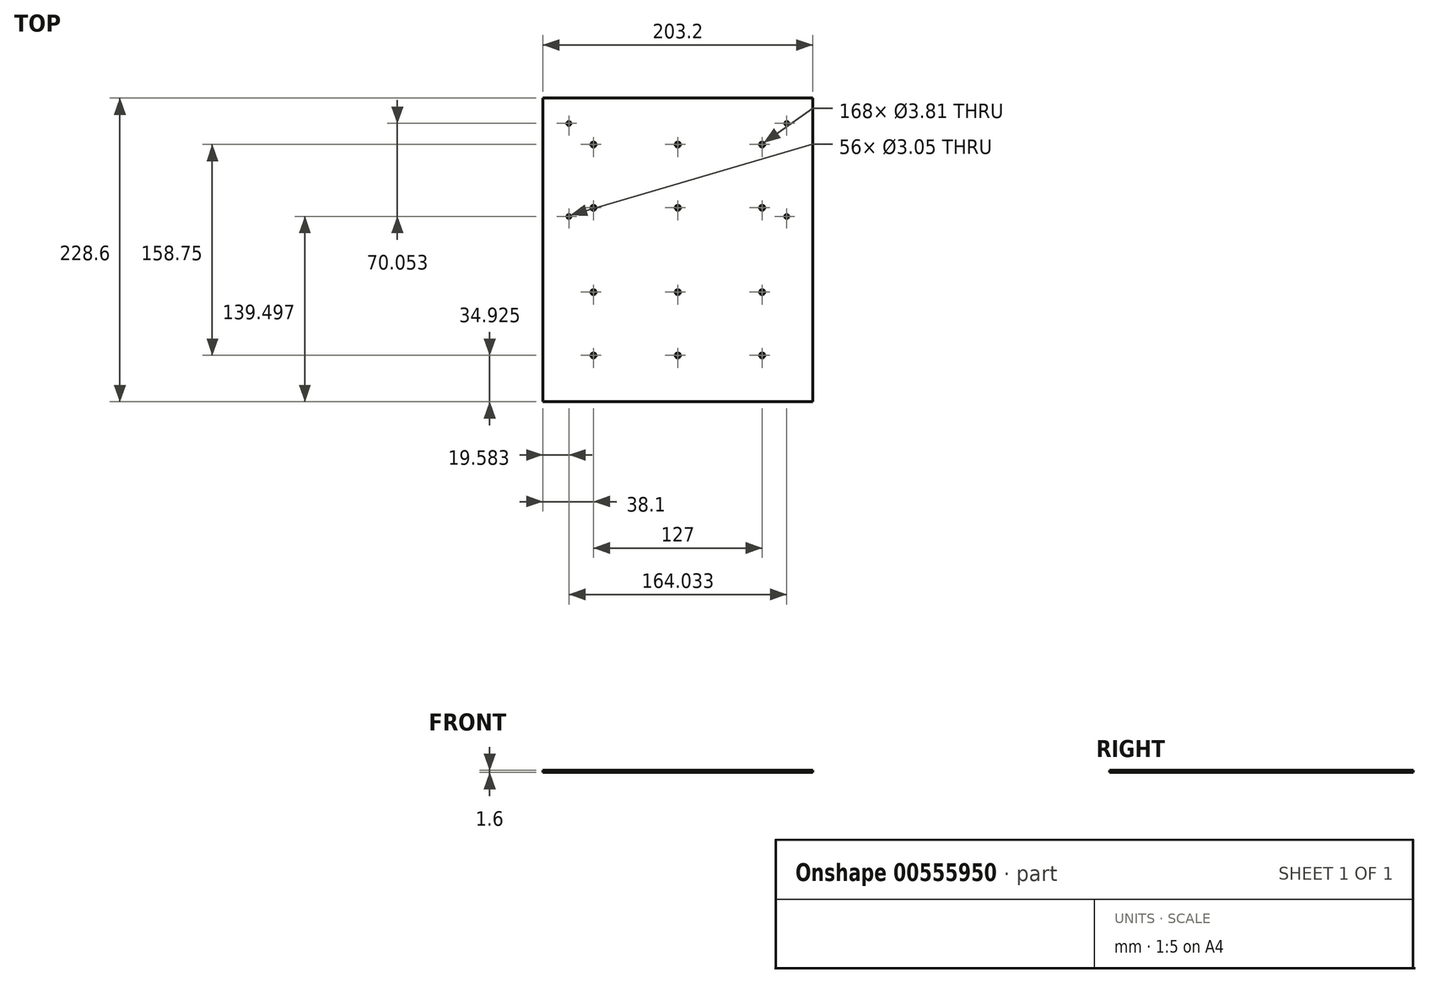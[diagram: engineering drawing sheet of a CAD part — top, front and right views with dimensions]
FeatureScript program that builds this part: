
annotation { "Feature Type Name" : "Feature", "Feature Type Description" : "" }
export const myFeature = defineFeature(function(context is Context, id is Id, definition is map)
    precondition{}
    {
        {
            var Q0;
            Q0=qCreatedBy(makeId("Top.planeOp"),FACE);
            var sketch = newSketch(context, id + "F0", { "sketchPlane" : qUnion([Q0])});
            skLineSegment(sketch, "E0.bottom", {"start": v(0, 0) * mm, "end": v(203.2, 0) * mm});
            skLineSegment(sketch, "E0.top", {"start": v(0, 228.6) * mm, "end": v(203.2, 228.6) * mm});
            skLineSegment(sketch, "E0.left", {"start": v(0, 0) * mm, "end": v(0, 228.6) * mm});
            skLineSegment(sketch, "E0.right", {"start": v(203.2, 0) * mm, "end": v(203.2, 228.6) * mm});
            skSolve(sketch);
        }
        {
            var Q0;
            Q0=makeQuery(id+"F0.imprint","IMPRINT",FACE,{"disambiguationData":[TD([[makeQuery(id+"F0.imprint","IMPRINT",EDGE,{"derivedFrom":sQuery(id+"F0.wireOp",EDGE,"E0.bottom")}),1.0]])]});
            extrude(context, id + "F1", {"entities" : qUnion([Q0]), "depth" : 1.6 * mm, "offsetDistance" : 25.4 * mm});
        }
        {
            var Q0;
            Q0=makeQuery(id+"F1.opExtrude","CAP_FACE",FACE,{"disambiguationData":[OSD([sQuery(id+"F0.wireOp",EDGE,"E0.bottom"),sQuery(id+"F0.wireOp",EDGE,"E0.top"),sQuery(id+"F0.wireOp",EDGE,"E0.left"),sQuery(id+"F0.wireOp",EDGE,"E0.right")])],"isStart":false});
            var sketch = newSketch(context, id + "F2", { "sketchPlane" : qUnion([Q0])});
            skCircle(sketch, "E1", {"center": v(19.58, 209.55) * mm, "radius": 1.52 * mm});
            skCircle(sketch, "E2", {"center": v(183.62, 209.55) * mm, "radius": 1.52 * mm});
            skCircle(sketch, "E3", {"center": v(19.58, 139.5) * mm, "radius": 1.52 * mm});
            skCircle(sketch, "E4", {"center": v(183.62, 139.5) * mm, "radius": 1.52 * mm});
            skSolve(sketch);
        }
        {
            var Q0;
            Q0 = qSketchRegion(id + "F2", true);
            extrude(context, id + "F3", {"entities" : qUnion([Q0]), "operationType" : NewBodyOperationType.REMOVE, "endBound" : BoundingType.THROUGH_ALL, "oppositeDirection" : true, "depth" : 25.4 * mm, "offsetDistance" : 25.4 * mm});
        }
        {
            var Q0;
            Q0=makeQuery(id+"F1.opExtrude","CAP_FACE",FACE,{"disambiguationData":[OSD([sQuery(id+"F0.wireOp",EDGE,"E0.bottom"),sQuery(id+"F0.wireOp",EDGE,"E0.top"),sQuery(id+"F0.wireOp",EDGE,"E0.left"),sQuery(id+"F0.wireOp",EDGE,"E0.right")])],"isStart":false});
            var sketch = newSketch(context, id + "F4", { "sketchPlane" : qUnion([Q0])});
            skCircle(sketch, "E5", {"center": v(165.1, 34.93) * mm, "radius": 1.9 * mm});
            skCircle(sketch, "E6.0.1.0", {"center": v(165.1, 82.55) * mm, "radius": 1.9 * mm});
            skCircle(sketch, "E6.1.0.0", {"center": v(101.6, 34.93) * mm, "radius": 1.9 * mm});
            skCircle(sketch, "E6.1.1.0", {"center": v(101.6, 82.55) * mm, "radius": 1.9 * mm});
            skCircle(sketch, "E6.2.0.0", {"center": v(38.1, 34.93) * mm, "radius": 1.9 * mm});
            skCircle(sketch, "E6.2.1.0", {"center": v(38.1, 82.55) * mm, "radius": 1.9 * mm});
            skLineSegment(sketch, "E6.direction1", {"start": v(165.1, 34.93) * mm, "end": v(101.6, 34.93) * mm, "construction": true});
            skLineSegment(sketch, "E6.direction2", {"start": v(165.1, 34.93) * mm, "end": v(165.1, 82.55) * mm, "construction": true});
            skCircle(sketch, "E7", {"center": v(165.1, 146.05) * mm, "radius": 1.9 * mm});
            skCircle(sketch, "E8", {"center": v(101.6, 146.05) * mm, "radius": 1.9 * mm});
            skCircle(sketch, "E9", {"center": v(38.1, 146.05) * mm, "radius": 1.9 * mm});
            skCircle(sketch, "E10", {"center": v(38.1, 193.68) * mm, "radius": 1.9 * mm});
            skCircle(sketch, "E11", {"center": v(101.6, 193.68) * mm, "radius": 1.9 * mm});
            skCircle(sketch, "E12", {"center": v(165.1, 193.68) * mm, "radius": 1.9 * mm});
            skSolve(sketch);
        }
        {
            var Q0;
            Q0 = qSketchRegion(id + "F4", true);
            extrude(context, id + "F5", {"entities" : qUnion([Q0]), "operationType" : NewBodyOperationType.REMOVE, "endBound" : BoundingType.THROUGH_ALL, "oppositeDirection" : true, "depth" : 25.4 * mm, "offsetDistance" : 25.4 * mm});
        }
    });
